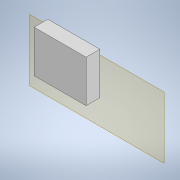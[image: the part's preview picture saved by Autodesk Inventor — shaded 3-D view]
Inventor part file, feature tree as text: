
AUTODESK INVENTOR PART (.ipt)
format: ipt  version: 2021 (Build 250183000, 183)  size: 94,208 bytes
history: native  units: mm
features: other x2, plane x1, extrude x1, sketch x1
ambient origin geometry x8: Origin, YZ Plane, XZ Plane, XY Plane, X Axis, Y Axis, Z Axis, Center Point
bodies: Solid1 (feature_tree)
feature tree (5):
  plane  "Work Plane1"
  extrude  "Extrusion1"  Depth=55.0mm
  sketch  "Sketch1"  dims[d0=68.0mm d1=55.0mm d2=18.0mm d3=0.0mm]
  other  "4_WheelsSwerve01.iam"
  other  "Part10"
